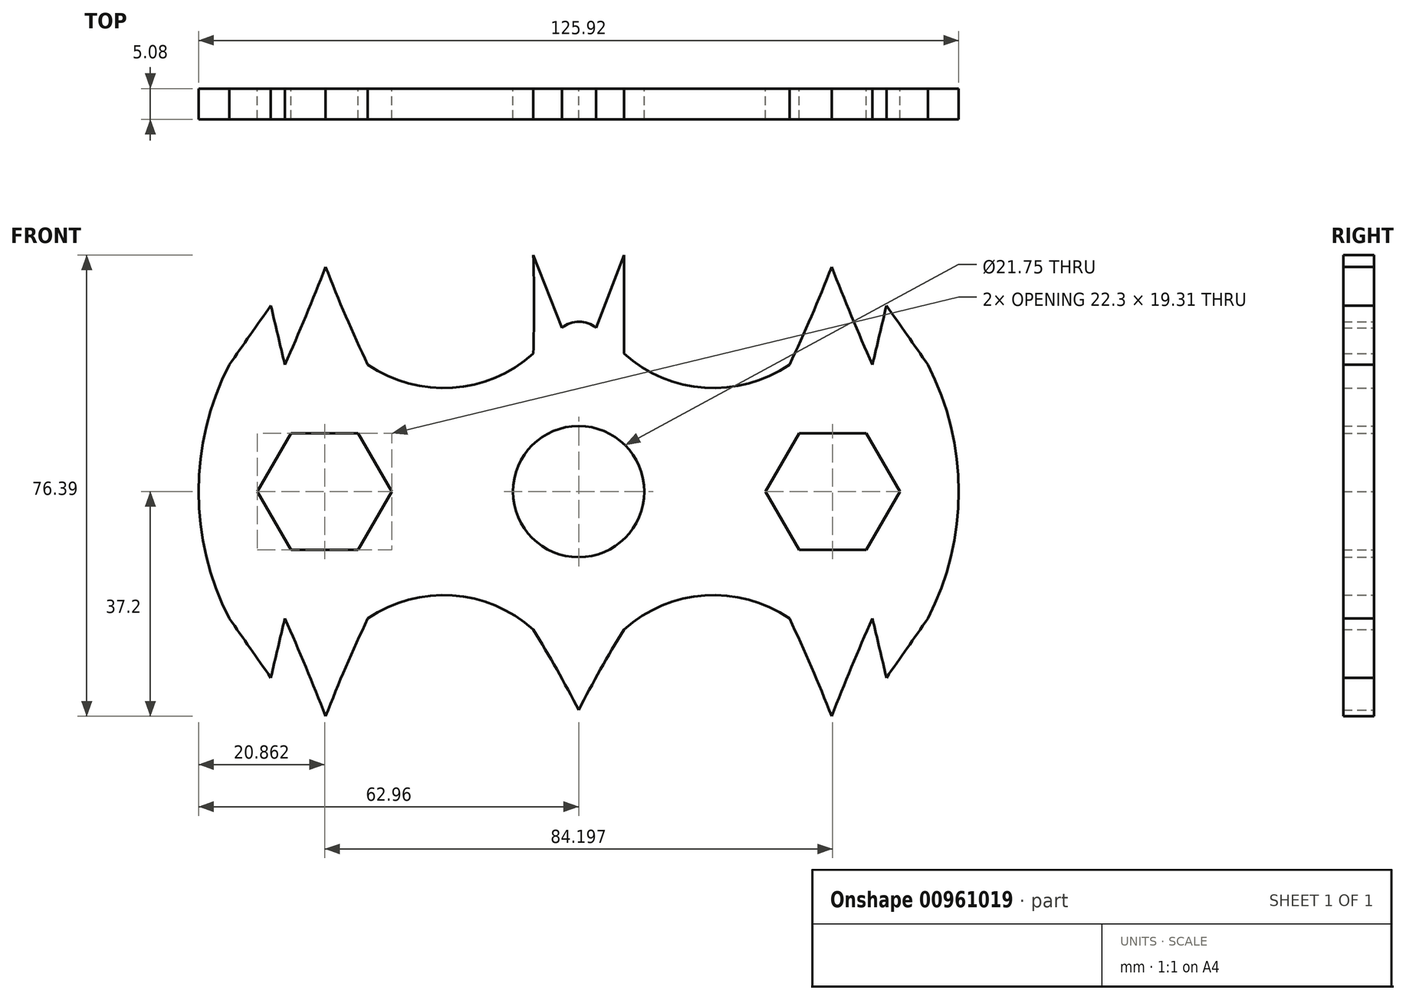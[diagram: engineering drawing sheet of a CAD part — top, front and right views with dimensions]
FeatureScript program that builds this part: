
annotation { "Feature Type Name" : "Feature", "Feature Type Description" : "" }
export const myFeature = defineFeature(function(context is Context, id is Id, definition is map)
    precondition{}
    {
        {
            var Q0;
            Q0=qCreatedBy(makeId("Front.planeOp"),FACE);
            var sketch = newSketch(context, id + "F0", { "sketchPlane" : qUnion([Q0])});
            skArc(sketch, "E0", {"start": v(0, -36.22) * mm, "mid": v(-3.61, -29.46) * mm, "end": v(-7.5, -22.86) * mm});
            skArc(sketch, "E1.MirrorCS", {"start": v(0, -36.22) * mm, "mid": v(3.61, -29.46) * mm, "end": v(7.5, -22.86) * mm});
            skArc(sketch, "E2", {"start": v(-7.5, -22.86) * mm, "mid": v(-20.9, -17.2) * mm, "end": v(-34.95, -21.02) * mm});
            skArc(sketch, "E3", {"start": v(-34.95, -21.02) * mm, "mid": v(-38.57, -29.05) * mm, "end": v(-41.93, -37.2) * mm});
            skArc(sketch, "E4", {"start": v(-41.93, -37.2) * mm, "mid": v(-45.2, -29.07) * mm, "end": v(-48.67, -21.02) * mm});
            skArc(sketch, "E5", {"start": v(-48.67, -21.02) * mm, "mid": v(-49.84, -25.92) * mm, "end": v(-51, -30.82) * mm});
            skArc(sketch, "E6", {"start": v(-57.86, -21.02) * mm, "mid": v(-54.44, -25.93) * mm, "end": v(-51, -30.82) * mm});
            skArc(sketch, "E7.MirrorCS", {"start": v(7.5, -22.86) * mm, "mid": v(20.9, -17.2) * mm, "end": v(34.95, -21.02) * mm});
            skArc(sketch, "E8.MirrorCS", {"start": v(34.95, -21.02) * mm, "mid": v(38.57, -29.05) * mm, "end": v(41.93, -37.2) * mm});
            skArc(sketch, "E9.MirrorCS", {"start": v(41.93, -37.2) * mm, "mid": v(45.2, -29.07) * mm, "end": v(48.67, -21.02) * mm});
            skArc(sketch, "E10.MirrorCS", {"start": v(48.67, -21.02) * mm, "mid": v(49.84, -25.92) * mm, "end": v(51, -30.82) * mm});
            skArc(sketch, "E11.MirrorCS", {"start": v(57.86, -21.02) * mm, "mid": v(54.44, -25.93) * mm, "end": v(51, -30.82) * mm});
            skArc(sketch, "E12.MirrorCS", {"start": v(-41.93, 37.2) * mm, "mid": v(-45.2, 29.07) * mm, "end": v(-48.67, 21.02) * mm});
            skArc(sketch, "E13.MirrorCS", {"start": v(-48.67, 21.02) * mm, "mid": v(-49.84, 25.92) * mm, "end": v(-51, 30.82) * mm});
            skArc(sketch, "E14.MirrorCS", {"start": v(-57.86, 21.02) * mm, "mid": v(-54.44, 25.93) * mm, "end": v(-51, 30.82) * mm});
            skArc(sketch, "E15.MirrorCS", {"start": v(-34.95, 21.02) * mm, "mid": v(-38.57, 29.05) * mm, "end": v(-41.93, 37.2) * mm});
            skArc(sketch, "E16.MirrorCS", {"start": v(-7.5, 22.86) * mm, "mid": v(-20.9, 17.2) * mm, "end": v(-34.95, 21.02) * mm});
            skArc(sketch, "E17.MirrorCS", {"start": v(7.5, 22.86) * mm, "mid": v(20.9, 17.2) * mm, "end": v(34.95, 21.02) * mm});
            skArc(sketch, "E18.MirrorCS", {"start": v(34.95, 21.02) * mm, "mid": v(38.57, 29.05) * mm, "end": v(41.93, 37.2) * mm});
            skArc(sketch, "E19.MirrorCS", {"start": v(41.93, 37.2) * mm, "mid": v(45.2, 29.07) * mm, "end": v(48.67, 21.02) * mm});
            skArc(sketch, "E20.MirrorCS", {"start": v(48.67, 21.02) * mm, "mid": v(49.84, 25.92) * mm, "end": v(51, 30.82) * mm});
            skArc(sketch, "E21.MirrorCS", {"start": v(57.86, 21.02) * mm, "mid": v(54.44, 25.93) * mm, "end": v(51, 30.82) * mm});
            skArc(sketch, "E22", {"start": v(-57.86, 21.02) * mm, "mid": v(-62.96, 0) * mm, "end": v(-57.86, -21.02) * mm});
            skArc(sketch, "E23.MirrorCS", {"start": v(57.86, 21.02) * mm, "mid": v(62.96, 0) * mm, "end": v(57.86, -21.02) * mm});
            skArc(sketch, "E24", {"start": v(-7.5, 22.86) * mm, "mid": v(-7.4, 31.03) * mm, "end": v(-7.5, 39.2) * mm});
            skLineSegment(sketch, "E25", {"start": v(-7.5, 39.2) * mm, "end": v(-2.77, 27.1) * mm});
            skLineSegment(sketch, "E26", {"start": v(7.5, 22.86) * mm, "end": v(7.5, 39.2) * mm});
            skLineSegment(sketch, "E27", {"start": v(7.5, 39.2) * mm, "end": v(2.9, 27.1) * mm});
            skArc(sketch, "E28", {"start": v(2.9, 27.1) * mm, "mid": v(0.07, 28.12) * mm, "end": v(-2.77, 27.1) * mm});
            skPoint(sketch, "E29.0.midPoint", {"position": v(-34.7, 10.1) * mm});
            skLineSegment(sketch, "E30.0", {"start": v(36.52, 9.66) * mm, "end": v(47.67, 9.66) * mm});
            skLineSegment(sketch, "E30.1", {"start": v(47.67, 9.66) * mm, "end": v(53.25, 0) * mm});
            skLineSegment(sketch, "E30.2", {"start": v(53.25, 0) * mm, "end": v(47.67, -9.66) * mm});
            skLineSegment(sketch, "E30.3", {"start": v(47.67, -9.66) * mm, "end": v(36.52, -9.66) * mm});
            skLineSegment(sketch, "E30.4", {"start": v(36.52, -9.66) * mm, "end": v(30.95, 0) * mm});
            skLineSegment(sketch, "E30.5", {"start": v(30.95, 0) * mm, "end": v(36.52, 9.66) * mm});
            skPoint(sketch, "E30.0.midPoint", {"position": v(42.1, 9.66) * mm});
            skLineSegment(sketch, "E31.MirrorCS", {"start": v(-36.52, 9.66) * mm, "end": v(-47.67, 9.66) * mm});
            skLineSegment(sketch, "E32.MirrorCS", {"start": v(-30.95, 0) * mm, "end": v(-36.52, 9.66) * mm});
            skLineSegment(sketch, "E33.MirrorCS", {"start": v(-36.52, -9.66) * mm, "end": v(-30.95, 0) * mm});
            skLineSegment(sketch, "E34.MirrorCS", {"start": v(-47.67, -9.66) * mm, "end": v(-36.52, -9.66) * mm});
            skLineSegment(sketch, "E35.MirrorCS", {"start": v(-53.25, 0) * mm, "end": v(-47.67, -9.66) * mm});
            skLineSegment(sketch, "E36.MirrorCS", {"start": v(-47.67, 9.66) * mm, "end": v(-53.25, 0) * mm});
            skCircle(sketch, "E37", {"center": v(0, 0) * mm, "radius": 10.87 * mm});
            skSolve(sketch);
        }
        {
            var Q0;
            Q0 = qSketchRegion(id + "F0", true);
            extrude(context, id + "F1", {"entities" : qUnion([Q0]), "depth" : 5.08 * mm, "offsetDistance" : 25.4 * mm});
        }
    });
